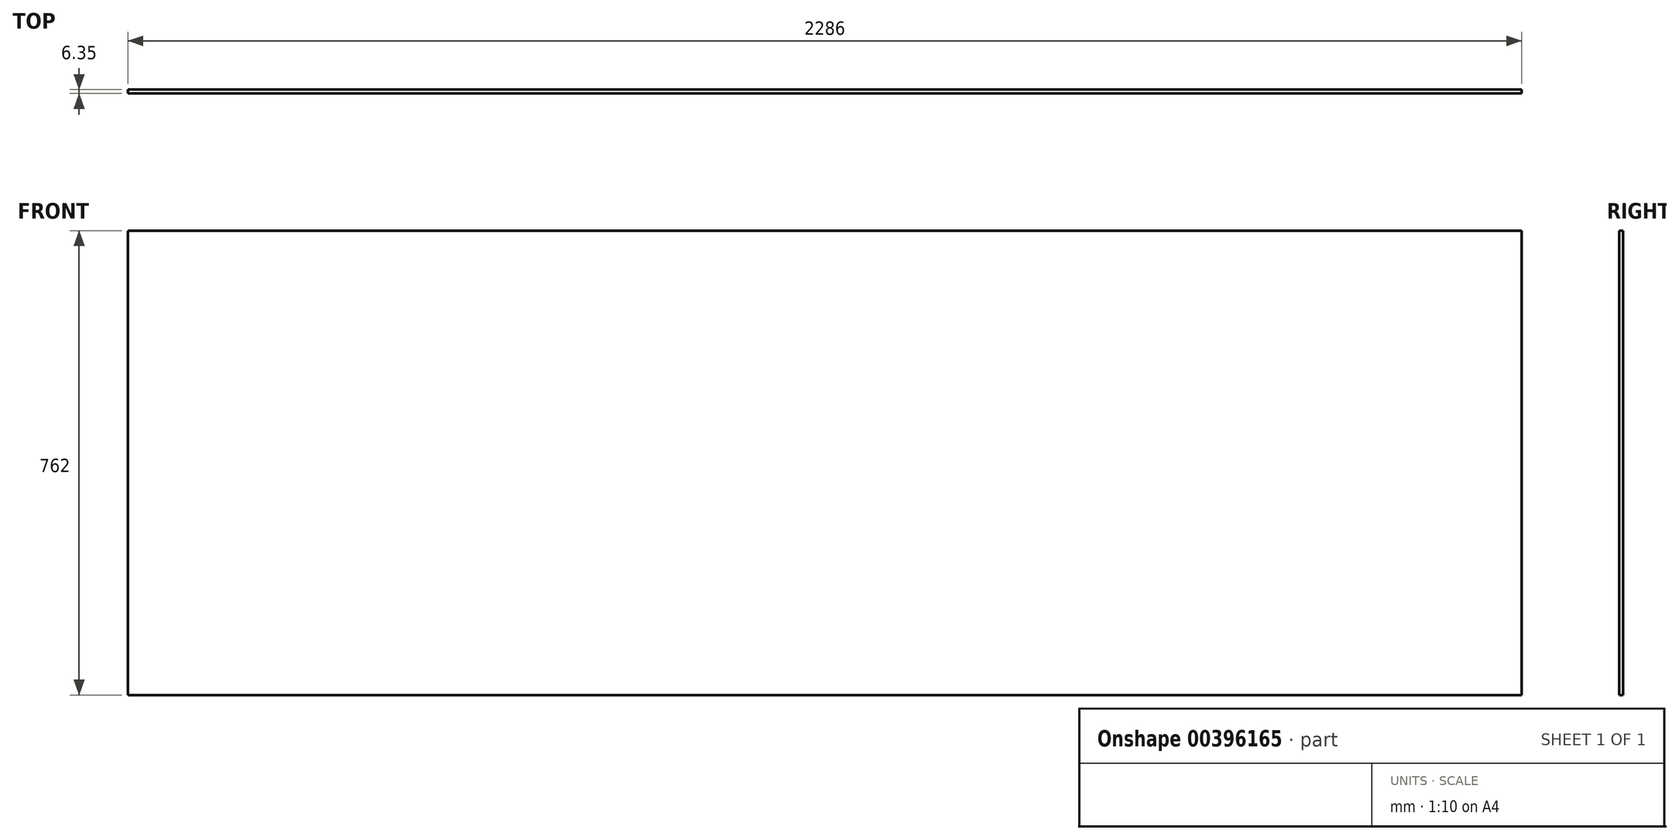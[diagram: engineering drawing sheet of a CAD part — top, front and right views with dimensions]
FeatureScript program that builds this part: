
annotation { "Feature Type Name" : "Feature", "Feature Type Description" : "" }
export const myFeature = defineFeature(function(context is Context, id is Id, definition is map)
    precondition{}
    {
        {
            var Q0;
            Q0=qCreatedBy(makeId("Right.planeOp"),FACE);
            var sketch = newSketch(context, id + "F0", { "sketchPlane" : qUnion([Q0])});
            skLineSegment(sketch, "E0.bottom", {"start": v(-68.35, -50.19) * mm, "end": v(-74.7, -50.19) * mm});
            skLineSegment(sketch, "E0.top", {"start": v(-68.35, 711.81) * mm, "end": v(-74.7, 711.81) * mm});
            skLineSegment(sketch, "E0.left", {"start": v(-68.35, -50.19) * mm, "end": v(-68.35, 711.81) * mm});
            skLineSegment(sketch, "E0.right", {"start": v(-74.7, -50.19) * mm, "end": v(-74.7, 711.81) * mm});
            skPoint(sketch, "E0.middle", {"position": v(-71.53, 330.81) * mm});
            skSolve(sketch);
        }
        {
            var Q0;
            Q0=makeQuery(id+"F0.imprint","IMPRINT",FACE,{"disambiguationData":[TD([[makeQuery(id+"F0.imprint","IMPRINT",EDGE,{"derivedFrom":sQuery(id+"F0.wireOp",EDGE,"E0.bottom")}),-1.0]])]});
            extrude(context, id + "F1", {"entities" : qUnion([Q0]), "depth" : 2286 * mm});
        }
    });
